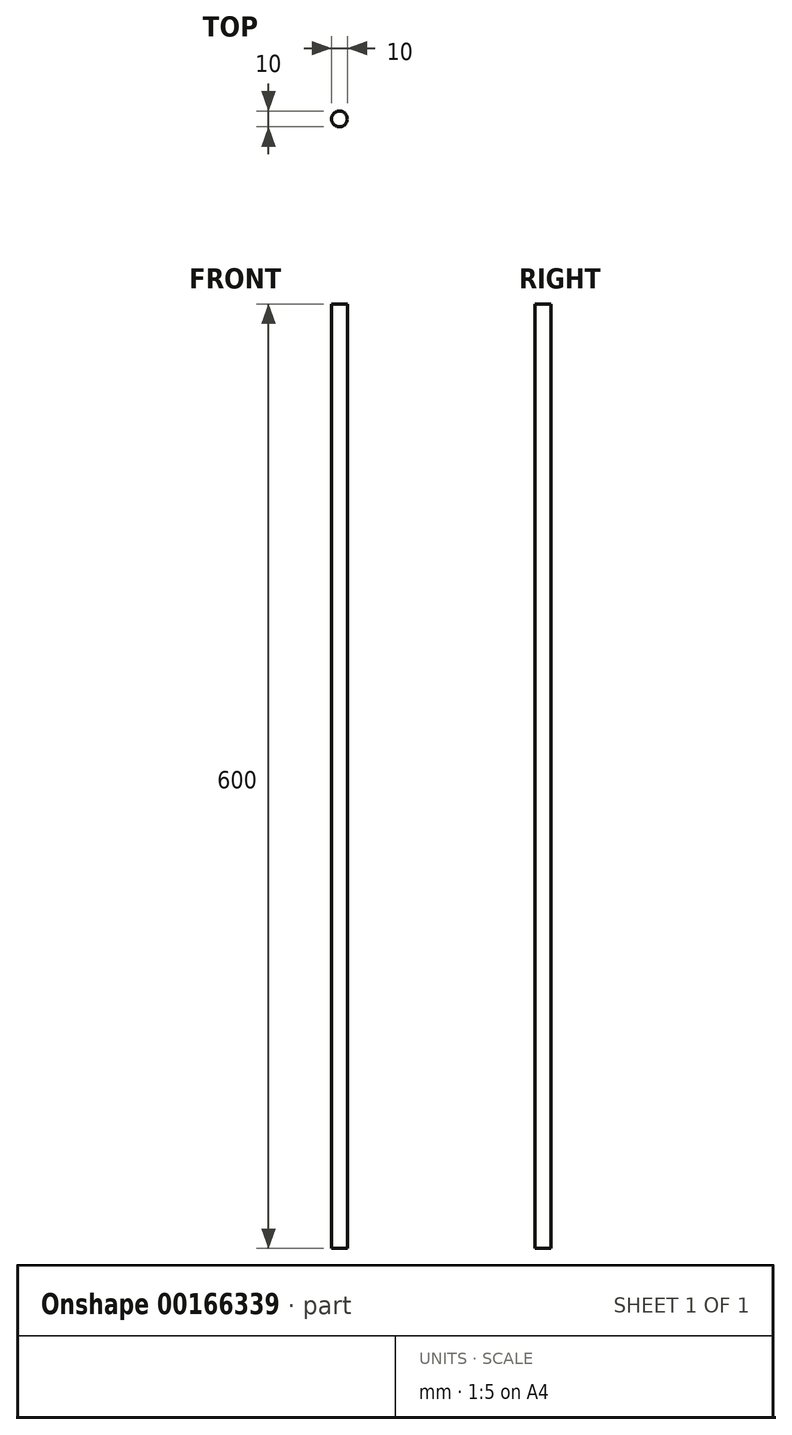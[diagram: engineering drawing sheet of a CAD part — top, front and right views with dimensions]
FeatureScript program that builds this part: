
annotation { "Feature Type Name" : "Feature", "Feature Type Description" : "" }
export const myFeature = defineFeature(function(context is Context, id is Id, definition is map)
    precondition{}
    {
        {
            var Q0;
            Q0=qCreatedBy(makeId("Top.planeOp"),FACE);
            var sketch = newSketch(context, id + "F0", { "sketchPlane" : qUnion([Q0])});
            skCircle(sketch, "E0", {"center": v(0, 0) * mm, "radius": 5 * mm});
            skSolve(sketch);
        }
        {
            var Q0;
            Q0 = qSketchRegion(id + "F0", true);
            extrude(context, id + "F1", {"entities" : qUnion([Q0]), "depth" : 600 * mm});
        }
    });
